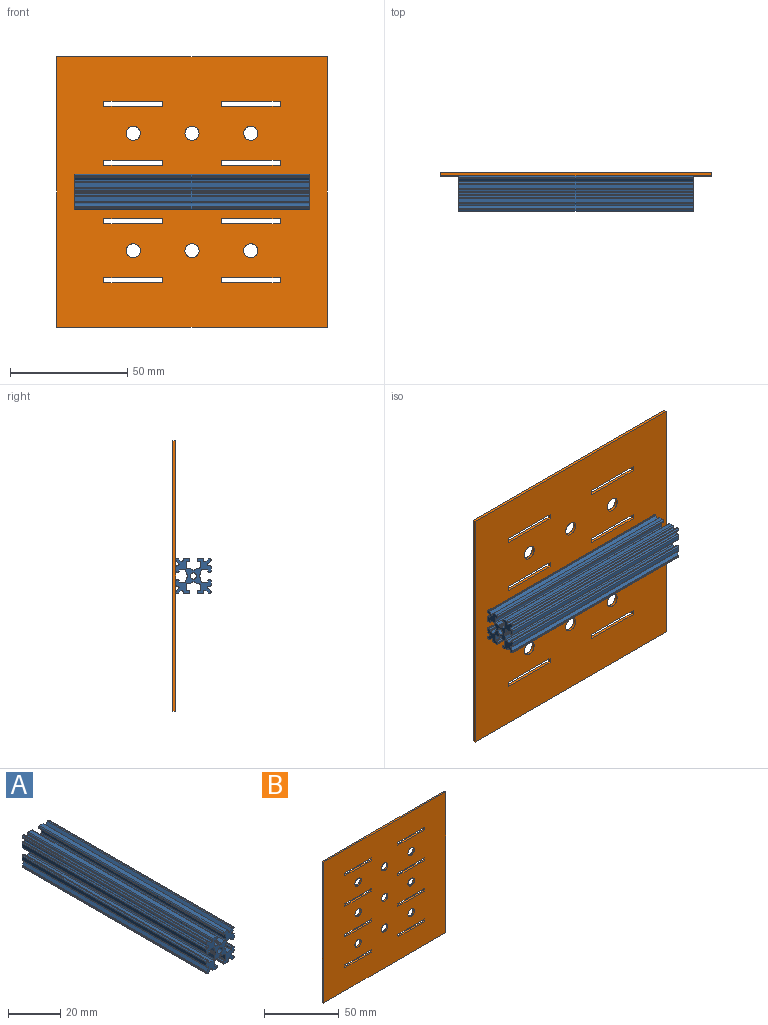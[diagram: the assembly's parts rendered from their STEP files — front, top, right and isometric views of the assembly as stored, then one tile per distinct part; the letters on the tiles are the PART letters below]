
ASSEMBLY  parts=2 mates=1
PART A: 155 faces, bbox 15x100x15 mm
  f0: plane 100x0.28mm, normal (-1,0,0), area 28.3mm2, adj f1,f152,f153,f154
  f1: cylinder r=0.5mm len=100mm, axis (0,1,0), area 78.5mm2, adj f0,f2,f153,f154
  f2: plane 100x0.28mm, normal (0,0,-1), area 28.3mm2, adj f1,f3,f153,f154
  f3: cylinder r=0.5mm len=100mm, axis (0,1,0), area 39.3mm2, adj f2,f4,f153,f154
  f4: plane 100x1.11mm, normal (0.71,0,-0.71), area 156.6mm2, adj f3,f5,f153,f154
  f5: cylinder r=0.5mm len=100mm, axis (0,1,0), area 117.8mm2, adj f4,f6,f153,f154
  f6: plane 100x0.4mm, normal (-1,0,0), area 40mm2, adj f5,f7,f153,f154
  f7: cylinder r=0.5mm len=100mm, axis (0,1,0), area 78.5mm2, adj f6,f8,f153,f154
  f8: plane 100x1.8mm, normal (0,0,-1), area 180.3mm2, adj f7,f9,f153,f154
  f9: cylinder r=0.5mm len=100mm, axis (0,1,0), area 78.5mm2, adj f8,f10,f153,f154
  f10: plane 100x0.4mm, normal (1,0,0), area 40mm2, adj f9,f11,f153,f154
  f11: cylinder r=0.5mm len=100mm, axis (0,1,0), area 78.5mm2, adj f10,f12,f153,f154
  f12: plane 100x0.6mm, normal (0,0,1), area 60mm2, adj f11,f13,f153,f154
  f13: cylinder r=0.2mm len=100mm, axis (0,1,0), area 31.4mm2, adj f12,f14,f153,f154
  f14: plane 100x2.16mm, normal (1,0,0), area 216.2mm2, adj f13,f15,f153,f154
  f15: cylinder r=0.5mm len=100mm, axis (0,1,0), area 69.6mm2, adj f14,f16,f153,f154
  f16: plane 100x1.75mm, normal (0.18,0,-0.98), area 178.2mm2, adj f15,f17,f153,f154
  f17: cylinder r=0.2mm len=100mm, axis (0,1,0), area 27.8mm2, adj f16,f18,f153,f154
  f18: plane 100x0.13mm, normal (1,0,0), area 13.3mm2, adj f17,f19,f153,f154
  f19: cylinder r=0.2mm len=100mm, axis (0,1,0), area 31.4mm2, adj f18,f20,f153,f154
  f20: plane 100x0.74mm, normal (0,0,-1), area 74mm2, adj f19,f21,f153,f154
  f21: cylinder r=0.2mm len=100mm, axis (0,1,0), area 31.4mm2, adj f20,f22,f153,f154
  f22: plane 100x0.13mm, normal (-1,0,0), area 13.3mm2, adj f21,f23,f153,f154
  f23: cylinder r=0.2mm len=100mm, axis (0,1,0), area 27.8mm2, adj f22,f24,f153,f154
  f24: plane 100x1.75mm, normal (-0.18,0,-0.98), area 178.2mm2, adj f23,f25,f153,f154
  f25: cylinder r=0.5mm len=100mm, axis (0,1,0), area 69.6mm2, adj f24,f26,f153,f154
  f26: plane 100x2.16mm, normal (-1,0,0), area 216.2mm2, adj f25,f27,f153,f154
  f27: cylinder r=0.2mm len=100mm, axis (0,1,0), area 31.4mm2, adj f26,f28,f153,f154
  f28: plane 100x0.6mm, normal (0,0,1), area 60mm2, adj f27,f29,f153,f154
  f29: cylinder r=0.5mm len=100mm, axis (0,1,0), area 78.5mm2, adj f28,f30,f153,f154
  f30: plane 100x0.4mm, normal (-1,0,0), area 40mm2, adj f29,f31,f153,f154
  f31: cylinder r=0.5mm len=100mm, axis (0,1,0), area 78.5mm2, adj f30,f32,f153,f154
  f32: plane 100x1.8mm, normal (0,0,-1), area 180.3mm2, adj f31,f33,f153,f154
  f33: cylinder r=0.5mm len=100mm, axis (0,1,0), area 78.5mm2, adj f32,f34,f153,f154
  f34: plane 100x0.4mm, normal (1,0,0), area 40mm2, adj f33,f35,f153,f154
  f35: cylinder r=0.5mm len=100mm, axis (0,1,0), area 117.8mm2, adj f34,f36,f153,f154
  f36: plane 100x1.11mm, normal (-0.71,0,-0.71), area 156.6mm2, adj f35,f37,f153,f154
  f37: cylinder r=0.5mm len=100mm, axis (0,1,0), area 39.3mm2, adj f36,f38,f153,f154
  f38: plane 100x0.28mm, normal (0,0,-1), area 28.3mm2, adj f37,f39,f153,f154
  f39: cylinder r=0.5mm len=100mm, axis (0,1,0), area 78.5mm2, adj f38,f40,f153,f154
  f40: plane 100x0.28mm, normal (1,0,0), area 28.3mm2, adj f39,f41,f153,f154
  f41: cylinder r=0.5mm len=100mm, axis (0,1,0), area 39.3mm2, adj f40,f42,f153,f154
  f42: plane 100x1.11mm, normal (0.71,0,0.71), area 156.6mm2, adj f41,f43,f153,f154
  f43: cylinder r=0.5mm len=100mm, axis (0,1,0), area 117.8mm2, adj f42,f44,f153,f154
  f44: plane 100x0.4mm, normal (0,0,-1), area 40mm2, adj f43,f45,f153,f154
  f45: cylinder r=0.5mm len=100mm, axis (0,1,0), area 78.5mm2, adj f44,f46,f153,f154
  f46: plane 100x1.8mm, normal (1,0,0), area 180.3mm2, adj f45,f47,f153,f154
  f47: cylinder r=0.5mm len=100mm, axis (0,1,0), area 78.5mm2, adj f46,f48,f153,f154
  f48: plane 100x0.4mm, normal (0,0,1), area 40mm2, adj f47,f49,f153,f154
  f49: cylinder r=0.5mm len=100mm, axis (0,1,0), area 78.5mm2, adj f48,f50,f153,f154
  f50: plane 100x0.6mm, normal (-1,0,0), area 60mm2, adj f49,f51,f153,f154
  f51: cylinder r=0.2mm len=100mm, axis (0,1,0), area 31.4mm2, adj f50,f52,f153,f154
  f52: plane 100x2.16mm, normal (0,0,1), area 216.2mm2, adj f51,f53,f153,f154
  f53: cylinder r=0.5mm len=100mm, axis (0,1,0), area 69.6mm2, adj f52,f54,f153,f154
  f54: plane 100x1.75mm, normal (0.98,0,0.18), area 178.2mm2, adj f53,f55,f153,f154
  f55: cylinder r=0.2mm len=100mm, axis (0,1,0), area 27.8mm2, adj f54,f56,f153,f154
  f56: plane 100x0.13mm, normal (0,0,1), area 13.3mm2, adj f55,f57,f153,f154
  f57: cylinder r=0.2mm len=100mm, axis (0,1,0), area 31.4mm2, adj f56,f58,f153,f154
  f58: plane 100x0.74mm, normal (1,0,0), area 74mm2, adj f57,f59,f153,f154
  f59: cylinder r=0.2mm len=100mm, axis (0,1,0), area 31.4mm2, adj f58,f60,f153,f154
  f60: plane 100x0.13mm, normal (0,0,-1), area 13.3mm2, adj f59,f61,f153,f154
  f61: cylinder r=0.2mm len=100mm, axis (0,1,0), area 27.8mm2, adj f60,f62,f153,f154
  f62: plane 100x1.75mm, normal (0.98,0,-0.18), area 178.2mm2, adj f61,f63,f153,f154
  f63: cylinder r=0.5mm len=100mm, axis (0,1,0), area 69.6mm2, adj f62,f64,f153,f154
  f64: plane 100x2.16mm, normal (0,0,-1), area 216.2mm2, adj f63,f65,f153,f154
  f65: cylinder r=0.2mm len=100mm, axis (0,1,0), area 31.4mm2, adj f64,f66,f153,f154
  f66: plane 100x0.6mm, normal (-1,0,0), area 60mm2, adj f65,f67,f153,f154
  f67: cylinder r=0.5mm len=100mm, axis (0,1,0), area 78.5mm2, adj f66,f68,f153,f154
  f68: plane 100x0.4mm, normal (0,0,-1), area 40mm2, adj f67,f69,f153,f154
  f69: cylinder r=0.5mm len=100mm, axis (0,1,0), area 78.5mm2, adj f68,f70,f153,f154
  f70: plane 100x1.8mm, normal (1,0,0), area 180.3mm2, adj f69,f71,f153,f154
  f71: cylinder r=0.5mm len=100mm, axis (0,1,0), area 78.5mm2, adj f70,f72,f153,f154
  f72: plane 100x0.4mm, normal (0,0,1), area 40mm2, adj f71,f73,f153,f154
  f73: cylinder r=0.5mm len=100mm, axis (0,1,0), area 117.8mm2, adj f72,f74,f153,f154
  f74: plane 100x1.11mm, normal (0.71,0,-0.71), area 156.6mm2, adj f73,f75,f153,f154
  f75: cylinder r=0.5mm len=100mm, axis (0,1,0), area 39.3mm2, adj f74,f76,f153,f154
  f76: plane 100x0.28mm, normal (1,0,0), area 28.3mm2, adj f75,f77,f153,f154
  f77: cylinder r=0.5mm len=100mm, axis (0,1,0), area 78.5mm2, adj f76,f78,f153,f154
  f78: plane 100x0.28mm, normal (0,0,1), area 28.3mm2, adj f77,f79,f153,f154
  f79: cylinder r=0.5mm len=100mm, axis (0,1,0), area 39.3mm2, adj f78,f80,f153,f154
  f80: plane 100x1.11mm, normal (-0.71,0,0.71), area 156.6mm2, adj f79,f81,f153,f154
  f81: cylinder r=0.5mm len=100mm, axis (0,1,0), area 117.8mm2, adj f80,f82,f153,f154
  f82: plane 100x0.4mm, normal (1,0,0), area 40mm2, adj f81,f83,f153,f154
  f83: cylinder r=0.5mm len=100mm, axis (0,1,0), area 78.5mm2, adj f82,f84,f153,f154
  f84: plane 100x1.8mm, normal (0,0,1), area 180.3mm2, adj f83,f85,f153,f154
  f85: cylinder r=0.5mm len=100mm, axis (0,1,0), area 78.5mm2, adj f84,f86,f153,f154
  f86: plane 100x0.4mm, normal (-1,0,0), area 40mm2, adj f85,f87,f153,f154
  f87: cylinder r=0.5mm len=100mm, axis (0,1,0), area 78.5mm2, adj f86,f88,f153,f154
  f88: plane 100x0.6mm, normal (0,0,-1), area 60mm2, adj f87,f89,f153,f154
  f89: cylinder r=0.2mm len=100mm, axis (0,1,0), area 31.4mm2, adj f88,f90,f153,f154
  f90: plane 100x2.16mm, normal (-1,0,0), area 216.2mm2, adj f89,f91,f153,f154
  f91: cylinder r=0.5mm len=100mm, axis (0,1,0), area 69.6mm2, adj f90,f92,f153,f154
  f92: plane 100x1.75mm, normal (-0.18,0,0.98), area 178.2mm2, adj f91,f93,f153,f154
  f93: cylinder r=0.2mm len=100mm, axis (0,1,0), area 27.8mm2, adj f92,f94,f153,f154
  f94: plane 100x0.13mm, normal (-1,0,0), area 13.3mm2, adj f93,f95,f153,f154
  f95: cylinder r=0.2mm len=100mm, axis (0,1,0), area 31.4mm2, adj f94,f96,f153,f154
  f96: plane 100x0.74mm, normal (0,0,1), area 74mm2, adj f95,f97,f153,f154
  f97: cylinder r=0.2mm len=100mm, axis (0,1,0), area 31.4mm2, adj f96,f98,f153,f154
  f98: plane 100x0.13mm, normal (1,0,0), area 13.3mm2, adj f97,f99,f153,f154
  f99: cylinder r=0.2mm len=100mm, axis (0,1,0), area 27.8mm2, adj f98,f100,f153,f154
  f100: plane 100x1.75mm, normal (0.18,0,0.98), area 178.2mm2, adj f99,f101,f153,f154
  f101: cylinder r=0.5mm len=100mm, axis (0,1,0), area 69.6mm2, adj f100,f102,f153,f154
  f102: plane 100x2.16mm, normal (1,0,0), area 216.2mm2, adj f101,f103,f153,f154
  f103: cylinder r=0.2mm len=100mm, axis (0,1,0), area 31.4mm2, adj f102,f104,f153,f154
  f104: plane 100x0.6mm, normal (0,0,-1), area 60mm2, adj f103,f105,f153,f154
  f105: cylinder r=0.5mm len=100mm, axis (0,1,0), area 78.5mm2, adj f104,f106,f153,f154
  f106: plane 100x0.4mm, normal (1,0,0), area 40mm2, adj f105,f107,f153,f154
  f107: cylinder r=0.5mm len=100mm, axis (0,1,0), area 78.5mm2, adj f106,f108,f153,f154
  f108: plane 100x1.8mm, normal (0,0,1), area 180.3mm2, adj f107,f109,f153,f154
  f109: cylinder r=0.5mm len=100mm, axis (0,1,0), area 78.5mm2, adj f108,f110,f153,f154
  f110: plane 100x0.4mm, normal (-1,0,0), area 40mm2, adj f109,f111,f153,f154
  f111: cylinder r=0.5mm len=100mm, axis (0,1,0), area 117.8mm2, adj f110,f112,f153,f154
  f112: plane 100x1.11mm, normal (0.71,0,0.71), area 156.6mm2, adj f111,f113,f153,f154
  f113: cylinder r=0.5mm len=100mm, axis (0,1,0), area 39.3mm2, adj f112,f114,f153,f154
  f114: plane 100x0.28mm, normal (0,0,1), area 28.3mm2, adj f113,f115,f153,f154
  f115: cylinder r=0.5mm len=100mm, axis (0,1,0), area 78.5mm2, adj f114,f116,f153,f154
  f116: plane 100x0.28mm, normal (-1,0,0), area 28.3mm2, adj f115,f117,f153,f154
  f117: cylinder r=0.5mm len=100mm, axis (0,1,0), area 39.3mm2, adj f116,f118,f153,f154
  f118: plane 100x1.11mm, normal (-0.71,0,-0.71), area 156.6mm2, adj f117,f119,f153,f154
  f119: cylinder r=0.5mm len=100mm, axis (0,1,0), area 117.8mm2, adj f118,f120,f153,f154
  f120: plane 100x0.4mm, normal (0,0,1), area 40mm2, adj f119,f121,f153,f154
  f121: cylinder r=0.5mm len=100mm, axis (0,1,0), area 78.5mm2, adj f120,f122,f153,f154
  f122: plane 100x1.8mm, normal (-1,0,0), area 180.3mm2, adj f121,f123,f153,f154
  f123: cylinder r=0.5mm len=100mm, axis (0,1,0), area 78.5mm2, adj f122,f124,f153,f154
  f124: plane 100x0.4mm, normal (0,0,-1), area 40mm2, adj f123,f125,f153,f154
  f125: cylinder r=0.5mm len=100mm, axis (0,1,0), area 78.5mm2, adj f124,f126,f153,f154
  f126: plane 100x0.6mm, normal (1,0,0), area 60mm2, adj f125,f127,f153,f154
  f127: cylinder r=0.2mm len=100mm, axis (0,1,0), area 31.4mm2, adj f126,f128,f153,f154
  f128: plane 100x2.16mm, normal (0,0,-1), area 216.2mm2, adj f127,f129,f153,f154
  f129: cylinder r=0.5mm len=100mm, axis (0,1,0), area 69.6mm2, adj f128,f130,f153,f154
  f130: plane 100x1.75mm, normal (-0.98,0,-0.18), area 178.2mm2, adj f129,f131,f153,f154
  f131: cylinder r=0.2mm len=100mm, axis (0,1,0), area 27.8mm2, adj f130,f132,f153,f154
  f132: plane 100x0.13mm, normal (0,0,-1), area 13.3mm2, adj f131,f133,f153,f154
  f133: cylinder r=0.2mm len=100mm, axis (0,1,0), area 31.4mm2, adj f132,f134,f153,f154
  f134: plane 100x0.74mm, normal (-1,0,0), area 74mm2, adj f133,f135,f153,f154
  f135: cylinder r=0.2mm len=100mm, axis (0,1,0), area 31.4mm2, adj f134,f136,f153,f154
  f136: plane 100x0.13mm, normal (0,0,1), area 13.3mm2, adj f135,f137,f153,f154
  f137: cylinder r=0.2mm len=100mm, axis (0,1,0), area 27.8mm2, adj f136,f138,f153,f154
  f138: plane 100x1.75mm, normal (-0.98,0,0.18), area 178.2mm2, adj f137,f139,f153,f154
  f139: cylinder r=0.5mm len=100mm, axis (0,1,0), area 69.6mm2, adj f138,f140,f153,f154
  f140: plane 100x2.16mm, normal (0,0,1), area 216.2mm2, adj f139,f141,f153,f154
  f141: cylinder r=0.2mm len=100mm, axis (0,1,0), area 31.4mm2, adj f140,f142,f153,f154
  f142: plane 100x0.6mm, normal (1,0,0), area 60mm2, adj f141,f143,f153,f154
  f143: cylinder r=0.5mm len=100mm, axis (0,1,0), area 78.5mm2, adj f142,f144,f153,f154
  f144: plane 100x0.4mm, normal (0,0,1), area 40mm2, adj f143,f145,f153,f154
  f145: cylinder r=0.5mm len=100mm, axis (0,1,0), area 78.5mm2, adj f144,f146,f153,f154
  f146: plane 100x1.8mm, normal (-1,0,0), area 180.3mm2, adj f145,f147,f153,f154
  f147: cylinder r=0.5mm len=100mm, axis (0,1,0), area 78.5mm2, adj f146,f148,f153,f154
  f148: plane 100x0.4mm, normal (0,0,-1), area 40mm2, adj f147,f149,f153,f154
  f149: cylinder r=0.5mm len=100mm, axis (0,1,0), area 117.8mm2, adj f148,f150,f153,f154
  f150: plane 100x1.11mm, normal (-0.71,0,0.71), area 156.6mm2, adj f149,f152,f153,f154
  f151: cylinder r=1.35mm len=100mm, axis (0,1,0), area 848.2mm2, adj f153,f154
  f152: cylinder r=0.5mm len=100mm, axis (0,1,0), area 39.3mm2, adj f0,f150,f153,f154
  f153: plane 15x15mm, normal (0,-1,0), area 112.3mm2, adj f0,f1,f2,f3,f4,f5,f6,f7
  f154: plane 15x15mm, normal (0,1,0), area 112.3mm2, adj f0,f1,f2,f3,f4,f5,f6,f7
PART B: 47 faces, bbox 115x1.2x115 mm
  f0: plane 115x1.2mm, normal (0,0,-1), area 138mm2, adj f1,f44,f45,f46
  f1: plane 115x1.2mm, normal (1,0,0), area 138mm2, adj f0,f2,f45,f46
  f2: plane 115x1.2mm, normal (0,0,1), area 138mm2, adj f1,f44,f45,f46
  f3: plane 25x1.2mm, normal (0,0,-1), area 30mm2, adj f4,f27,f45,f46
  f4: plane 2.2x1.2mm, normal (-1,0,0), area 2.6mm2, adj f3,f5,f45,f46
  f5: plane 25x1.2mm, normal (0,0,1), area 30mm2, adj f4,f27,f45,f46
  f6: plane 2.2x1.2mm, normal (1,0,0), area 2.6mm2, adj f7,f28,f45,f46
  f7: plane 25x1.2mm, normal (0,0,-1), area 30mm2, adj f6,f8,f45,f46
  f8: plane 2.2x1.2mm, normal (-1,0,0), area 2.6mm2, adj f7,f28,f45,f46
  f9: plane 2.2x1.2mm, normal (-1,0,0), area 2.6mm2, adj f10,f29,f45,f46
  f10: plane 25x1.2mm, normal (0,0,1), area 30mm2, adj f9,f11,f45,f46
  f11: plane 2.2x1.2mm, normal (1,0,0), area 2.6mm2, adj f10,f29,f45,f46
  f12: plane 2.2x1.2mm, normal (-1,0,0), area 2.6mm2, adj f13,f30,f45,f46
  f13: plane 25x1.2mm, normal (0,0,1), area 30mm2, adj f12,f14,f45,f46
  f14: plane 2.2x1.2mm, normal (1,0,0), area 2.6mm2, adj f13,f30,f45,f46
  f15: plane 2.2x1.2mm, normal (-1,0,0), area 2.6mm2, adj f16,f31,f45,f46
  f16: plane 25x1.2mm, normal (0,0,1), area 30mm2, adj f15,f17,f45,f46
  f17: plane 2.2x1.2mm, normal (1,0,0), area 2.6mm2, adj f16,f31,f45,f46
  f18: plane 2.2x1.2mm, normal (1,0,0), area 2.6mm2, adj f19,f41,f45,f46
  f19: plane 25x1.2mm, normal (0,0,-1), area 30mm2, adj f18,f20,f45,f46
  f20: plane 2.2x1.2mm, normal (-1,0,0), area 2.6mm2, adj f19,f41,f45,f46
  f21: plane 2.2x1.2mm, normal (1,0,0), area 2.6mm2, adj f22,f42,f45,f46
  f22: plane 25x1.2mm, normal (0,0,-1), area 30mm2, adj f21,f23,f45,f46
  f23: plane 2.2x1.2mm, normal (-1,0,0), area 2.6mm2, adj f22,f42,f45,f46
  f24: plane 25x1.2mm, normal (0,0,1), area 30mm2, adj f25,f43,f45,f46
  f25: plane 2.2x1.2mm, normal (1,0,0), area 2.6mm2, adj f24,f26,f45,f46
  f26: plane 25x1.2mm, normal (0,0,-1), area 30mm2, adj f25,f43,f45,f46
  f27: plane 2.2x1.2mm, normal (1,0,0), area 2.6mm2, adj f3,f5,f45,f46
  f28: plane 25x1.2mm, normal (0,0,1), area 30mm2, adj f6,f8,f45,f46
  f29: plane 25x1.2mm, normal (0,0,-1), area 30mm2, adj f9,f11,f45,f46
  f30: plane 25x1.2mm, normal (0,0,-1), area 30mm2, adj f12,f14,f45,f46
  f31: plane 25x1.2mm, normal (0,0,-1), area 30mm2, adj f15,f17,f45,f46
  f32: cylinder r=3mm len=6mm, axis (0,1,0), area 22.6mm2, adj f45,f46
  f33: cylinder r=3mm len=6mm, axis (0,1,0), area 22.6mm2, adj f45,f46
  f34: cylinder r=3mm len=6mm, axis (0,1,0), area 22.6mm2, adj f45,f46
  f35: cylinder r=3mm len=6mm, axis (0,1,0), area 22.6mm2, adj f45,f46
  f36: cylinder r=3mm len=6mm, axis (0,1,0), area 22.6mm2, adj f45,f46
  f37: cylinder r=3mm len=6mm, axis (0,1,0), area 22.6mm2, adj f45,f46
  f38: cylinder r=3mm len=6mm, axis (0,1,0), area 22.6mm2, adj f45,f46
  f39: cylinder r=3mm len=6mm, axis (0,1,0), area 22.6mm2, adj f45,f46
  f40: cylinder r=3mm len=6mm, axis (0,1,0), area 22.6mm2, adj f45,f46
  f41: plane 25x1.2mm, normal (0,0,1), area 30mm2, adj f18,f20,f45,f46
  f42: plane 25x1.2mm, normal (0,0,1), area 30mm2, adj f21,f23,f45,f46
  f43: plane 2.2x1.2mm, normal (-1,0,0), area 2.6mm2, adj f24,f26,f45,f46
  f44: plane 115x1.2mm, normal (-1,0,0), area 138mm2, adj f0,f2,f45,f46
  f45: plane 115x115mm, normal (0,-1,0), area 12530.5mm2, adj f0,f1,f2,f3,f4,f5,f6,f7
  f46: plane 115x115mm, normal (0,1,0), area 12530.5mm2, adj f0,f1,f2,f3,f4,f5,f6,f7
PLACE A rot(axis=(-0.71,0.71,0),180deg) t=(0,-8.7,0)mm
PLACE B at identity fixed
MATE fastened A.f122 <-> B.f34  axis (0,1,0) through (0,-1.2,0)mm
